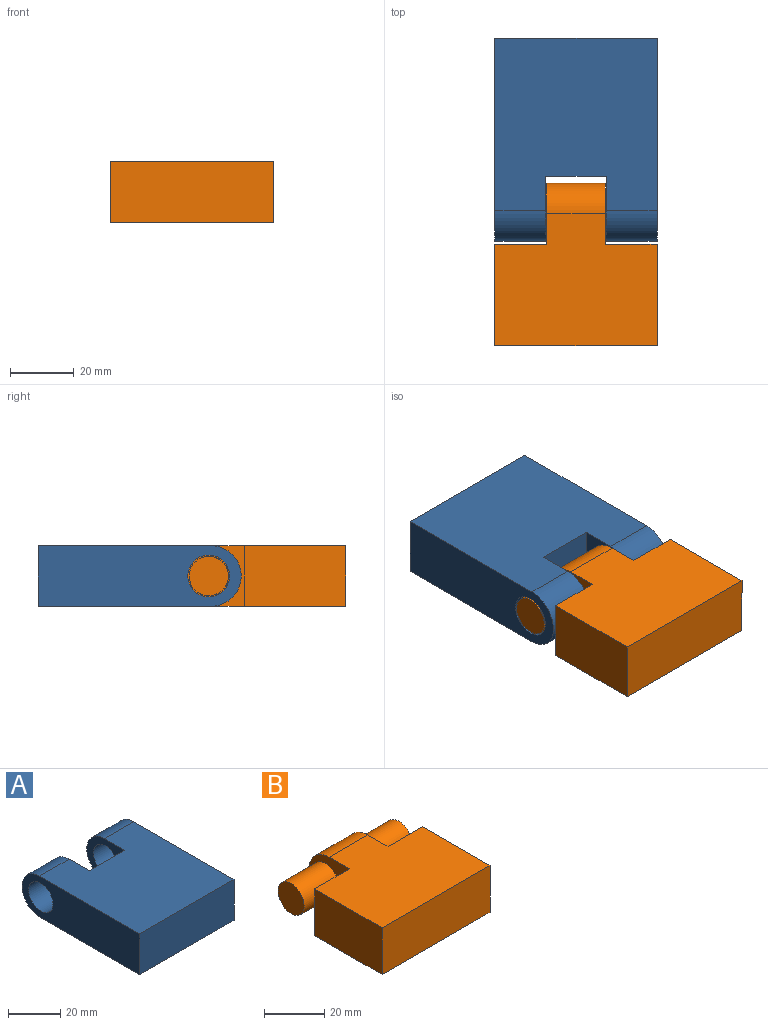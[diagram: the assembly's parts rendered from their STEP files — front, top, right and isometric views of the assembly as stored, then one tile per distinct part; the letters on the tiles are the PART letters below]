
ASSEMBLY  parts=2 mates=1
PART A: 12 faces, bbox 50.8x63.5x19.1 mm
  f0: plane 63.5x19.05mm, normal (-1,0,0), area 1036mm2, adj f1,f3,f4,f8,f11
  f1: plane 50.8x19.05mm, normal (0,-1,0), area 967.7mm2, adj f0,f2,f3,f4
  f2: plane 63.5x19.05mm, normal (1,0,0), area 1036mm2, adj f1,f3,f4,f9,f10
  f3: plane 53.98x50.8mm, normal (0,0,1), area 2536.3mm2, adj f0,f1,f2,f5,f6,f7,f10,f11
  f4: plane 53.98x50.8mm, normal (0,0,-1), area 2536.3mm2, adj f0,f1,f2,f5,f6,f7,f10,f11
  f5: plane 19.05x19.05mm, normal (0,1,0), area 362.9mm2, adj f3,f4,f6,f7
  f6: plane 20.32x19.05mm, normal (-1,0,0), area 213.4mm2, adj f3,f4,f5,f9,f10
  f7: plane 20.32x19.05mm, normal (1,0,0), area 213.4mm2, adj f3,f4,f5,f8,f11
  f8: cylinder r=6.55mm len=15.88mm, axis (-1,0,0), area 653.3mm2, adj f0,f7
  f9: cylinder r=6.55mm len=15.88mm, axis (-1,0,0), area 653.3mm2, adj f2,f6
  f10: cylinder r=9.53mm len=19.05mm, axis (-1,0,0), area 475mm2, adj f2,f3,f4,f6
  f11: cylinder r=9.53mm len=19.05mm, axis (1,0,0), area 475mm2, adj f0,f3,f4,f7
PART B: 14 faces, bbox 50.8x50.8x19.1 mm
  f0: plane 19.05x19.05mm, normal (-1,0,0), area 205.1mm2, adj f1,f7,f8,f11,f13
  f1: plane 19.05x16.28mm, normal (0,1,0), area 310.2mm2, adj f0,f2,f7,f8
  f2: plane 31.75x19.05mm, normal (-1,0,0), area 604.8mm2, adj f1,f3,f7,f8
  f3: plane 50.8x19.05mm, normal (0,-1,0), area 967.7mm2, adj f2,f4,f7,f8
  f4: plane 31.75x19.05mm, normal (1,0,0), area 604.8mm2, adj f3,f5,f7,f8
  f5: plane 19.05x16.27mm, normal (0,1,0), area 309.9mm2, adj f4,f6,f7,f8
  f6: plane 19.05x19.05mm, normal (1,0,0), area 205.1mm2, adj f5,f7,f8,f10,f13
  f7: plane 50.8x41.28mm, normal (0,0,1), area 1786.7mm2, adj f0,f1,f2,f3,f4,f5,f6,f13
  f8: plane 50.8x41.28mm, normal (0,0,-1), area 1786.7mm2, adj f0,f1,f2,f3,f4,f5,f6,f13
  f9: plane 12.3x12.3mm, normal (1,0,0), area 118.8mm2, adj f10
  f10: cylinder r=6.15mm len=16.27mm, axis (1,0,0), area 628.6mm2, adj f6,f9
  f11: cylinder r=6.15mm len=16.28mm, axis (1,0,0), area 629.1mm2, adj f0,f12
  f12: plane 12.3x12.3mm, normal (-1,0,0), area 118.8mm2, adj f11
  f13: cylinder r=9.53mm len=19.05mm, axis (1,0,0), area 546.1mm2, adj f0,f6,f7,f8
PLACE A rot(axis=(-1,0,0),180deg) t=(1.4,-38.43,9.85)mm
PLACE B rot(axis=(1,0,0),0deg) t=(-5.62,-24.43,-9.2)mm
MATE revolute A.f8 <-> B.f10  axis (1,0,0) through (29.22,-52.62,0.32)mm
